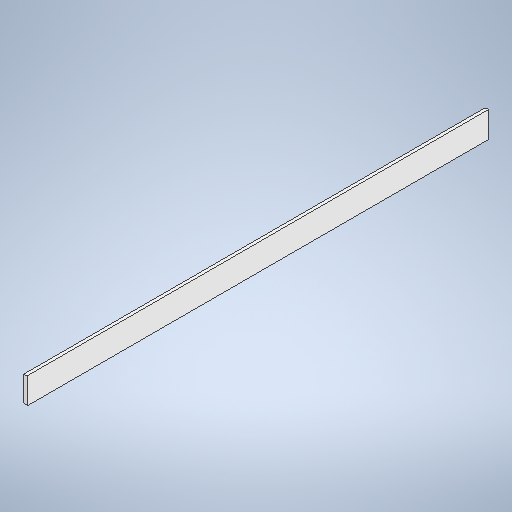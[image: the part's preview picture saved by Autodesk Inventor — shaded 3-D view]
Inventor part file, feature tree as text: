
AUTODESK INVENTOR PART (.ipt)
format: ipt  version: 2025 (Build 290162010, 162A)  size: 254,976 bytes
history: native  units: in
note: dims shown in document units (in); Inventor stores cm internally (conversion verified against a paired STEP export)
features: extrude x1, sketch x1
ambient origin geometry x8: Origin, YZ Plane, XZ Plane, XY Plane, X Axis, Y Axis, Z Axis, Center Point
bodies: Body1 (feature_tree)
feature tree (2):
  extrude  "Extrusion3"  Depth=97.504in
  sketch  "Sketch1"  dims[d33=42.875in d36=132.0in d37=3.5in d42=1.0in d43=5.5in d44=97.504in d45=0.0in]
